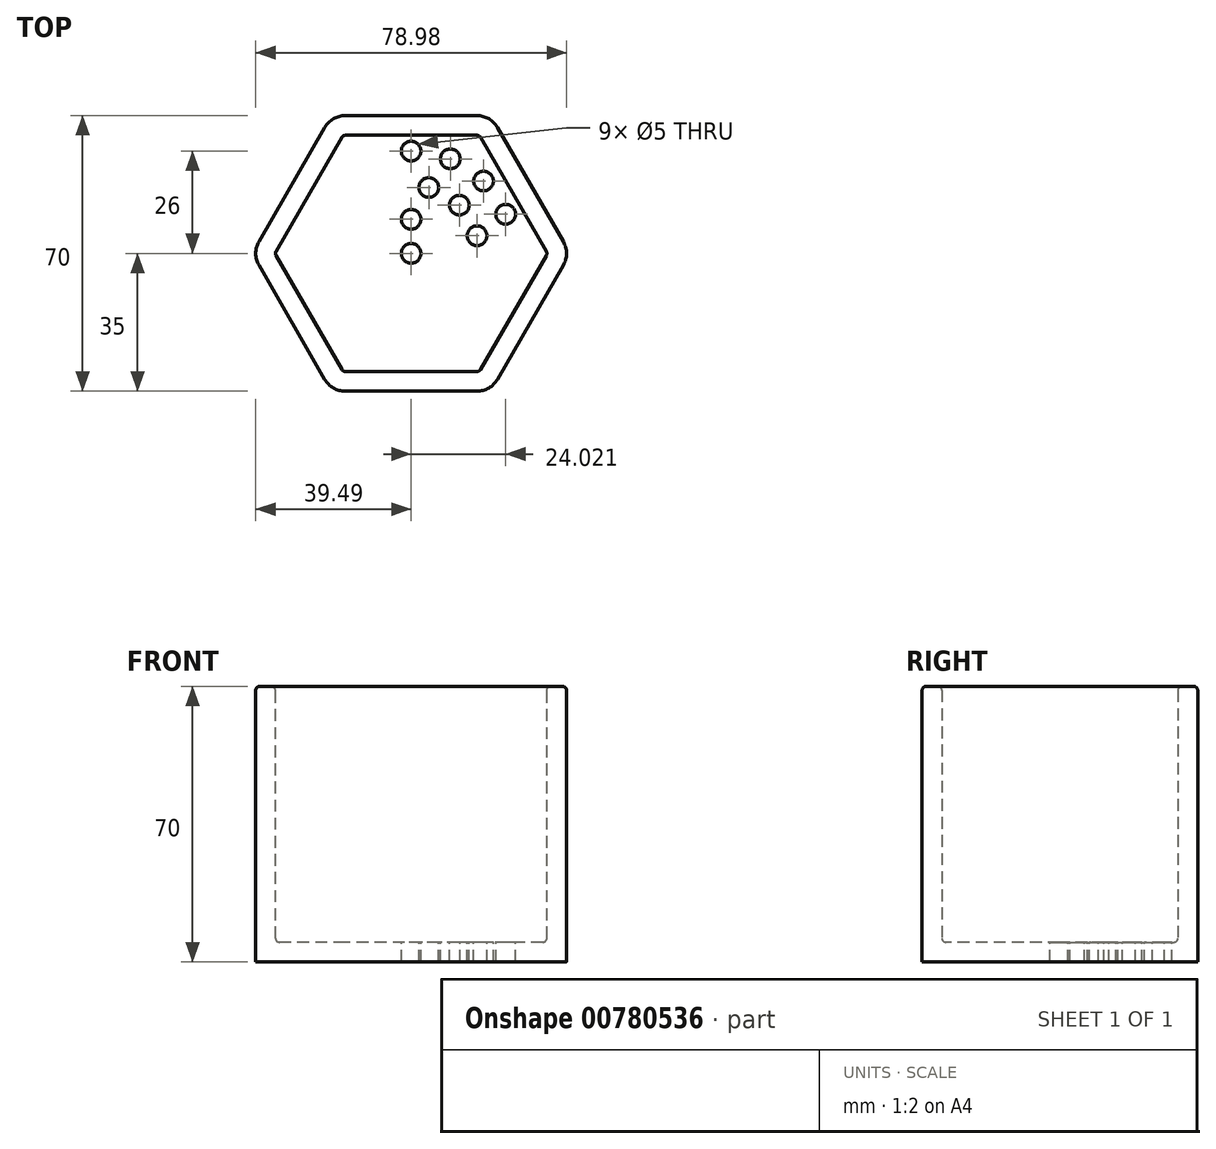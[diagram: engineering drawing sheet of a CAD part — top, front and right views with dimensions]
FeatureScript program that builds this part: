
annotation { "Feature Type Name" : "Feature", "Feature Type Description" : "" }
export const myFeature = defineFeature(function(context is Context, id is Id, definition is map)
    precondition{}
    {
        {
            var Q0;
            Q0=qCreatedBy(makeId("Top.planeOp"),FACE);
            var sketch = newSketch(context, id + "F0", { "sketchPlane" : qUnion([Q0])});
            skCircle(sketch, "E0.cCircle", {"center": v(0, 0) * mm, "radius": 35 * mm, "construction": true});
            skLineSegment(sketch, "E0.0", {"start": v(-20.2, 35) * mm, "end": v(20.2, 35) * mm});
            skLineSegment(sketch, "E0.1", {"start": v(20.2, 35) * mm, "end": v(40.41, 0) * mm});
            skLineSegment(sketch, "E0.2", {"start": v(40.41, 0) * mm, "end": v(20.2, -35) * mm});
            skLineSegment(sketch, "E0.3", {"start": v(20.2, -35) * mm, "end": v(-20.2, -35) * mm});
            skLineSegment(sketch, "E0.4", {"start": v(-20.2, -35) * mm, "end": v(-40.41, 0) * mm});
            skLineSegment(sketch, "E0.5", {"start": v(-40.41, 0) * mm, "end": v(-20.2, 35) * mm});
            skPoint(sketch, "E0.0.midPoint", {"position": v(0, 35) * mm});
            skLineSegment(sketch, "E1.0", {"start": v(-34.64, 0) * mm, "end": v(-17.32, 30) * mm});
            skLineSegment(sketch, "E1.1", {"start": v(17.32, 30) * mm, "end": v(34.64, 0) * mm});
            skLineSegment(sketch, "E1.2", {"start": v(34.64, 0) * mm, "end": v(17.32, -30) * mm});
            skLineSegment(sketch, "E1.3", {"start": v(-17.32, 30) * mm, "end": v(17.32, 30) * mm});
            skLineSegment(sketch, "E1.4", {"start": v(17.32, -30) * mm, "end": v(-17.32, -30) * mm});
            skLineSegment(sketch, "E1.5", {"start": v(-17.32, -30) * mm, "end": v(-34.64, 0) * mm});
            skSolve(sketch);
        }
        {
            var Q0;
            Q0 = qSketchRegion(id + "F0", true);
            extrude(context, id + "F1", {"entities" : qUnion([Q0]), "depth" : 70 * mm, "offsetDistance" : 25 * mm});
        }
        {
            var Q0;
            Q0=makeQuery(id+"F1.opExtrude","CAP_FACE",FACE,{"disambiguationData":[OSD([sQuery(id+"F0.wireOp",EDGE,"E0.0"),sQuery(id+"F0.wireOp",EDGE,"E0.1"),sQuery(id+"F0.wireOp",EDGE,"E0.2"),sQuery(id+"F0.wireOp",EDGE,"E0.3"),sQuery(id+"F0.wireOp",EDGE,"E0.4"),sQuery(id+"F0.wireOp",EDGE,"E0.5"),sQuery(id+"F0.wireOp",EDGE,"E1.0"),sQuery(id+"F0.wireOp",EDGE,"E1.1"),sQuery(id+"F0.wireOp",EDGE,"E1.2"),sQuery(id+"F0.wireOp",EDGE,"E1.3"),sQuery(id+"F0.wireOp",EDGE,"E1.4"),sQuery(id+"F0.wireOp",EDGE,"E1.5")])],"isStart":true});
            var sketch = newSketch(context, id + "F2", { "sketchPlane" : qUnion([Q0])});
            skLineSegment(sketch, "E2.0.0", {"start": v(-40.41, 0) * mm, "end": v(-20.2, -35) * mm});
            skLineSegment(sketch, "E2.0.1", {"start": v(-20.2, -35) * mm, "end": v(20.2, -35) * mm});
            skLineSegment(sketch, "E2.0.2", {"start": v(20.2, -35) * mm, "end": v(40.41, 0) * mm});
            skLineSegment(sketch, "E2.0.3", {"start": v(40.41, 0) * mm, "end": v(20.2, 35) * mm});
            skLineSegment(sketch, "E2.0.4", {"start": v(20.2, 35) * mm, "end": v(-20.2, 35) * mm});
            skLineSegment(sketch, "E2.0.5", {"start": v(-20.2, 35) * mm, "end": v(-40.41, 0) * mm});
            skSolve(sketch);
        }
        {
            var Q0;
            Q0 = qSketchRegion(id + "F2", true);
            extrude(context, id + "F3", {"entities" : qUnion([Q0]), "operationType" : NewBodyOperationType.ADD, "oppositeDirection" : true, "depth" : 5 * mm, "offsetDistance" : 25 * mm});
        }
        {
            var Q0;
            Q0=makeQuery(id+"F3.opExtrude","CAP_FACE",FACE,{"disambiguationData":[OSD([sQuery(id+"F2.wireOp",EDGE,"E2.0.0"),sQuery(id+"F2.wireOp",EDGE,"E2.0.1"),sQuery(id+"F2.wireOp",EDGE,"E2.0.2"),sQuery(id+"F2.wireOp",EDGE,"E2.0.3"),sQuery(id+"F2.wireOp",EDGE,"E2.0.4"),sQuery(id+"F2.wireOp",EDGE,"E2.0.5")])],"isStart":false});
            var sketch = newSketch(context, id + "F4", { "sketchPlane" : qUnion([Q0])});
            skCircle(sketch, "E3", {"center": v(0, 0) * mm, "radius": 8.67 * mm, "construction": true});
            skCircle(sketch, "E4", {"center": v(0, 0) * mm, "radius": 17.33 * mm, "construction": true});
            skCircle(sketch, "E5", {"center": v(0, 0) * mm, "radius": 26 * mm, "construction": true});
            skLineSegment(sketch, "E6", {"start": v(0, 0) * mm, "end": v(0, 8.67) * mm, "construction": true});
            skLineSegment(sketch, "E7", {"start": v(0, 8.67) * mm, "end": v(0, 17.33) * mm, "construction": true});
            skLineSegment(sketch, "E8", {"start": v(0, 17.33) * mm, "end": v(0, 26) * mm, "construction": true});
            skCircle(sketch, "E9", {"center": v(0, 26) * mm, "radius": 2.5 * mm});
            skCircle(sketch, "E10", {"center": v(4.49, 16.74) * mm, "radius": 2.5 * mm});
            skCircle(sketch, "E11", {"center": v(0, 8.67) * mm, "radius": 2.5 * mm});
            skLineSegment(sketch, "E12", {"start": v(0, 0) * mm, "end": v(26, 0) * mm, "construction": true});
            skCircle(sketch, "E13", {"center": v(8.67, 0) * mm, "radius": 2.5 * mm, "construction": true});
            skCircle(sketch, "E14", {"center": v(12.26, 12.26) * mm, "radius": 2.5 * mm});
            skCircle(sketch, "E15", {"center": v(9.95, 24.02) * mm, "radius": 2.5 * mm});
            skCircle(sketch, "E16", {"center": v(24.02, 9.95) * mm, "radius": 2.5 * mm});
            skCircle(sketch, "E17", {"center": v(26, 0) * mm, "radius": 2.5 * mm, "construction": true});
            skCircle(sketch, "E18", {"center": v(16.74, 4.49) * mm, "radius": 2.5 * mm});
            skLineSegment(sketch, "E19", {"start": v(0, 0) * mm, "end": v(12.26, 12.26) * mm, "construction": true});
            skLineSegment(sketch, "E20", {"start": v(0, 0) * mm, "end": v(9.95, 24.02) * mm, "construction": true});
            skCircle(sketch, "E21", {"center": v(18.38, 18.38) * mm, "radius": 2.5 * mm});
            skLineSegment(sketch, "E22", {"start": v(0, 0) * mm, "end": v(4.49, 16.74) * mm, "construction": true});
            skSolve(sketch);
        }
        {
            var Q0;
            Q0 = qSketchRegion(id + "F4", true);
            extrude(context, id + "F5", {"entities" : qUnion([Q0]), "operationType" : NewBodyOperationType.REMOVE, "endBound" : BoundingType.UP_TO_NEXT, "oppositeDirection" : true, "depth" : 25 * mm, "offsetDistance" : 25 * mm});
        }
        {
            var Q0;
            Q0=qCreatedBy(makeId("Right.planeOp"),FACE);
            var sketch = newSketch(context, id + "F6", { "sketchPlane" : qUnion([Q0])});
            skLineSegment(sketch, "E23", {"start": v(0, 0) * mm, "end": v(0, 69.98) * mm});
            skSolve(sketch);
        }
        {
            var Q0;
            Q0=makeQuery(id+"F3.opExtrude","CAP_FACE",FACE,{"disambiguationData":[OSD([sQuery(id+"F2.wireOp",EDGE,"E2.0.0"),sQuery(id+"F2.wireOp",EDGE,"E2.0.1"),sQuery(id+"F2.wireOp",EDGE,"E2.0.2"),sQuery(id+"F2.wireOp",EDGE,"E2.0.3"),sQuery(id+"F2.wireOp",EDGE,"E2.0.4"),sQuery(id+"F2.wireOp",EDGE,"E2.0.5")])],"isStart":false});
            var sketch = newSketch(context, id + "F7", { "sketchPlane" : qUnion([Q0])});
            skCircle(sketch, "E24", {"center": v(0, 0) * mm, "radius": 2.5 * mm});
            skSolve(sketch);
        }
        {
            var Q0;
            Q0 = qSketchRegion(id + "F7", true);
            extrude(context, id + "F8", {"entities" : qUnion([Q0]), "operationType" : NewBodyOperationType.REMOVE, "endBound" : BoundingType.UP_TO_NEXT, "oppositeDirection" : true, "depth" : 25 * mm, "offsetDistance" : 25 * mm});
        }
        {
            var Q0;
            Q0=makeQuery(id+"F1.opExtrude","SWEPT_EDGE",EDGE,{"disambiguationData":[OSD([sQuery(id+"F0.wireOp",EDGE,"E0.0"),sQuery(id+"F0.wireOp",EDGE,"E0.5")])]});
            var Q1;
            Q1=makeQuery(id+"F1.opExtrude","SWEPT_EDGE",EDGE,{"disambiguationData":[OSD([sQuery(id+"F0.wireOp",EDGE,"E0.4"),sQuery(id+"F0.wireOp",EDGE,"E0.5")])]});
            var Q2;
            Q2=makeQuery(id+"F1.opExtrude","SWEPT_EDGE",EDGE,{"disambiguationData":[OSD([sQuery(id+"F0.wireOp",EDGE,"E0.3"),sQuery(id+"F0.wireOp",EDGE,"E0.4")])]});
            var Q3;
            Q3=makeQuery(id+"F1.opExtrude","SWEPT_EDGE",EDGE,{"disambiguationData":[OSD([sQuery(id+"F0.wireOp",EDGE,"E0.2"),sQuery(id+"F0.wireOp",EDGE,"E0.3")])]});
            var Q4;
            Q4=makeQuery(id+"F1.opExtrude","SWEPT_EDGE",EDGE,{"disambiguationData":[OSD([sQuery(id+"F0.wireOp",EDGE,"E0.1"),sQuery(id+"F0.wireOp",EDGE,"E0.2")])]});
            var Q5;
            Q5=makeQuery(id+"F1.opExtrude","SWEPT_EDGE",EDGE,{"disambiguationData":[OSD([sQuery(id+"F0.wireOp",EDGE,"E0.0"),sQuery(id+"F0.wireOp",EDGE,"E0.1")])]});
            fillet(context, id + "F9", {"entities" : qUnion([Q0, Q1, Q2, Q3, Q4, Q5]), "tangentPropagation" : true, "radius" : 6 * mm, "defaultsChanged" : true, "vertexSettings" : [], "allowEdgeOverflow" : false});
        }
        {
            var Q0;
            Q0=makeQuery(id+"F1.opExtrude","SWEPT_EDGE",EDGE,{"disambiguationData":[OSD([sQuery(id+"F0.wireOp",EDGE,"E1.0"),sQuery(id+"F0.wireOp",EDGE,"E1.3")])]});
            var Q1;
            Q1=makeQuery(id+"F1.opExtrude","SWEPT_EDGE",EDGE,{"disambiguationData":[OSD([sQuery(id+"F0.wireOp",EDGE,"E1.1"),sQuery(id+"F0.wireOp",EDGE,"E1.3")])]});
            var Q2;
            Q2=makeQuery(id+"F1.opExtrude","SWEPT_EDGE",EDGE,{"disambiguationData":[OSD([sQuery(id+"F0.wireOp",EDGE,"E1.1"),sQuery(id+"F0.wireOp",EDGE,"E1.2")])]});
            var Q3;
            Q3=makeQuery(id+"F1.opExtrude","SWEPT_EDGE",EDGE,{"disambiguationData":[OSD([sQuery(id+"F0.wireOp",EDGE,"E1.2"),sQuery(id+"F0.wireOp",EDGE,"E1.4")])]});
            var Q4;
            Q4=makeQuery(id+"F1.opExtrude","SWEPT_EDGE",EDGE,{"disambiguationData":[OSD([sQuery(id+"F0.wireOp",EDGE,"E1.4"),sQuery(id+"F0.wireOp",EDGE,"E1.5")])]});
            var Q5;
            Q5=makeQuery(id+"F1.opExtrude","SWEPT_EDGE",EDGE,{"disambiguationData":[OSD([sQuery(id+"F0.wireOp",EDGE,"E1.0"),sQuery(id+"F0.wireOp",EDGE,"E1.5")])]});
            var Q6;
            Q6=makeQuery(id+"F3.boolean.opBoolean","INTERSECT",EDGE,{"derivedFrom":[makeQuery(id+"F1.opExtrude","SWEPT_FACE",FACE,{"disambiguationData":[OSD([sQuery(id+"F0.wireOp",EDGE,"E1.0")])]}),makeQuery(id+"F3.opExtrude","CAP_FACE",FACE,{"disambiguationData":[OSD([sQuery(id+"F2.wireOp",EDGE,"E2.0.0"),sQuery(id+"F2.wireOp",EDGE,"E2.0.1"),sQuery(id+"F2.wireOp",EDGE,"E2.0.2"),sQuery(id+"F2.wireOp",EDGE,"E2.0.3"),sQuery(id+"F2.wireOp",EDGE,"E2.0.4"),sQuery(id+"F2.wireOp",EDGE,"E2.0.5")])],"isStart":false})]});
            var Q7;
            Q7=makeQuery(id+"F3.boolean.opBoolean","INTERSECT",EDGE,{"derivedFrom":[makeQuery(id+"F1.opExtrude","SWEPT_FACE",FACE,{"disambiguationData":[OSD([sQuery(id+"F0.wireOp",EDGE,"E1.5")])]}),makeQuery(id+"F3.opExtrude","CAP_FACE",FACE,{"disambiguationData":[OSD([sQuery(id+"F2.wireOp",EDGE,"E2.0.0"),sQuery(id+"F2.wireOp",EDGE,"E2.0.1"),sQuery(id+"F2.wireOp",EDGE,"E2.0.2"),sQuery(id+"F2.wireOp",EDGE,"E2.0.3"),sQuery(id+"F2.wireOp",EDGE,"E2.0.4"),sQuery(id+"F2.wireOp",EDGE,"E2.0.5")])],"isStart":false})]});
            var Q8;
            Q8=makeQuery(id+"F3.boolean.opBoolean","INTERSECT",EDGE,{"derivedFrom":[makeQuery(id+"F1.opExtrude","SWEPT_FACE",FACE,{"disambiguationData":[OSD([sQuery(id+"F0.wireOp",EDGE,"E1.4")])]}),makeQuery(id+"F3.opExtrude","CAP_FACE",FACE,{"disambiguationData":[OSD([sQuery(id+"F2.wireOp",EDGE,"E2.0.0"),sQuery(id+"F2.wireOp",EDGE,"E2.0.1"),sQuery(id+"F2.wireOp",EDGE,"E2.0.2"),sQuery(id+"F2.wireOp",EDGE,"E2.0.3"),sQuery(id+"F2.wireOp",EDGE,"E2.0.4"),sQuery(id+"F2.wireOp",EDGE,"E2.0.5")])],"isStart":false})]});
            var Q9;
            Q9=makeQuery(id+"F3.boolean.opBoolean","INTERSECT",EDGE,{"derivedFrom":[makeQuery(id+"F1.opExtrude","SWEPT_FACE",FACE,{"disambiguationData":[OSD([sQuery(id+"F0.wireOp",EDGE,"E1.2")])]}),makeQuery(id+"F3.opExtrude","CAP_FACE",FACE,{"disambiguationData":[OSD([sQuery(id+"F2.wireOp",EDGE,"E2.0.0"),sQuery(id+"F2.wireOp",EDGE,"E2.0.1"),sQuery(id+"F2.wireOp",EDGE,"E2.0.2"),sQuery(id+"F2.wireOp",EDGE,"E2.0.3"),sQuery(id+"F2.wireOp",EDGE,"E2.0.4"),sQuery(id+"F2.wireOp",EDGE,"E2.0.5")])],"isStart":false})]});
            var Q10;
            Q10=makeQuery(id+"F3.boolean.opBoolean","INTERSECT",EDGE,{"derivedFrom":[makeQuery(id+"F1.opExtrude","SWEPT_FACE",FACE,{"disambiguationData":[OSD([sQuery(id+"F0.wireOp",EDGE,"E1.1")])]}),makeQuery(id+"F3.opExtrude","CAP_FACE",FACE,{"disambiguationData":[OSD([sQuery(id+"F2.wireOp",EDGE,"E2.0.0"),sQuery(id+"F2.wireOp",EDGE,"E2.0.1"),sQuery(id+"F2.wireOp",EDGE,"E2.0.2"),sQuery(id+"F2.wireOp",EDGE,"E2.0.3"),sQuery(id+"F2.wireOp",EDGE,"E2.0.4"),sQuery(id+"F2.wireOp",EDGE,"E2.0.5")])],"isStart":false})]});
            var Q11;
            Q11=makeQuery(id+"F3.boolean.opBoolean","INTERSECT",EDGE,{"derivedFrom":[makeQuery(id+"F1.opExtrude","SWEPT_FACE",FACE,{"disambiguationData":[OSD([sQuery(id+"F0.wireOp",EDGE,"E1.3")])]}),makeQuery(id+"F3.opExtrude","CAP_FACE",FACE,{"disambiguationData":[OSD([sQuery(id+"F2.wireOp",EDGE,"E2.0.0"),sQuery(id+"F2.wireOp",EDGE,"E2.0.1"),sQuery(id+"F2.wireOp",EDGE,"E2.0.2"),sQuery(id+"F2.wireOp",EDGE,"E2.0.3"),sQuery(id+"F2.wireOp",EDGE,"E2.0.4"),sQuery(id+"F2.wireOp",EDGE,"E2.0.5")])],"isStart":false})]});
            fillet(context, id + "F10", {"entities" : qUnion([Q0, Q1, Q2, Q3, Q4, Q5, Q6, Q7, Q8, Q9, Q10, Q11]), "tangentPropagation" : true, "radius" : 1 * mm, "defaultsChanged" : false, "vertexSettings" : [], "allowEdgeOverflow" : false});
        }
        {
            var Q0;
            Q0=makeQuery(id+"F1.opExtrude","CAP_FACE",FACE,{"disambiguationData":[OSD([sQuery(id+"F0.wireOp",EDGE,"E0.0"),sQuery(id+"F0.wireOp",EDGE,"E0.1"),sQuery(id+"F0.wireOp",EDGE,"E0.2"),sQuery(id+"F0.wireOp",EDGE,"E0.3"),sQuery(id+"F0.wireOp",EDGE,"E0.4"),sQuery(id+"F0.wireOp",EDGE,"E0.5"),sQuery(id+"F0.wireOp",EDGE,"E1.0"),sQuery(id+"F0.wireOp",EDGE,"E1.1"),sQuery(id+"F0.wireOp",EDGE,"E1.2"),sQuery(id+"F0.wireOp",EDGE,"E1.3"),sQuery(id+"F0.wireOp",EDGE,"E1.4"),sQuery(id+"F0.wireOp",EDGE,"E1.5")])],"isStart":false});
            fillet(context, id + "F11", {"entities" : qUnion([Q0]), "tangentPropagation" : true, "radius" : 1 * mm, "defaultsChanged" : true, "vertexSettings" : [], "allowEdgeOverflow" : false});
        }
    });
